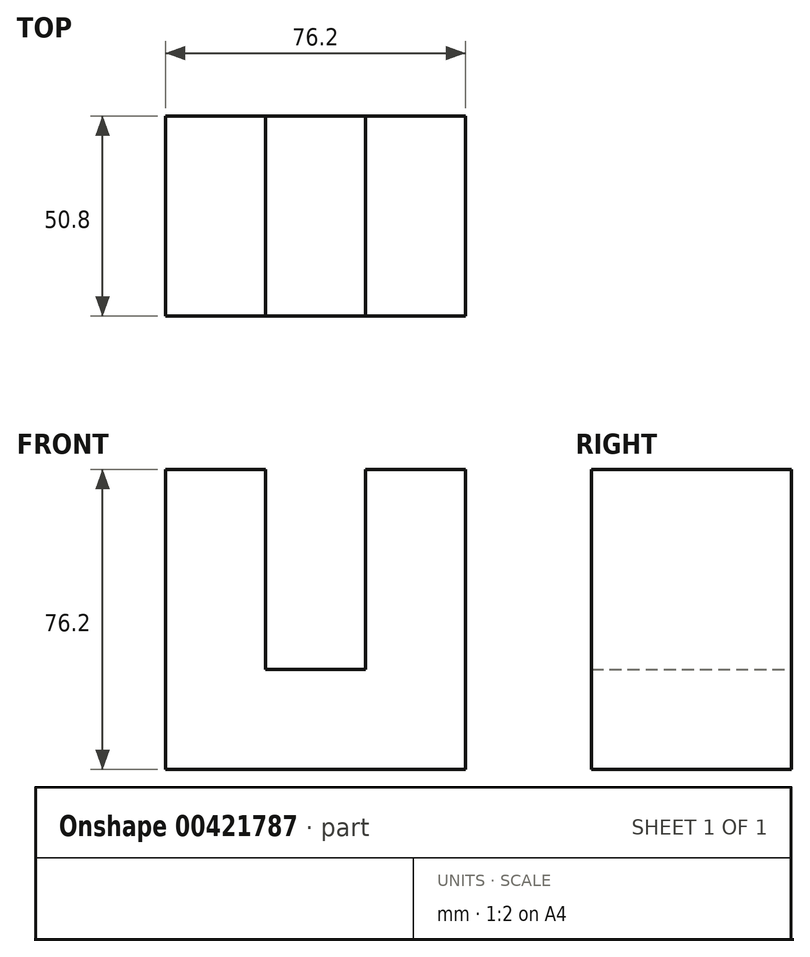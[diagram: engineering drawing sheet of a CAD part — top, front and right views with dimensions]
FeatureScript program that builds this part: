
annotation { "Feature Type Name" : "Feature", "Feature Type Description" : "" }
export const myFeature = defineFeature(function(context is Context, id is Id, definition is map)
    precondition{}
    {
        {
            var Q0;
            Q0=qCreatedBy(makeId("Front.planeOp"),FACE);
            var sketch = newSketch(context, id + "F0", { "sketchPlane" : qUnion([Q0])});
            skLineSegment(sketch, "E0", {"start": v(0, 0) * mm, "end": v(76.2, 0) * mm});
            skLineSegment(sketch, "E1", {"start": v(0, 0) * mm, "end": v(0, 76.2) * mm});
            skLineSegment(sketch, "E2", {"start": v(76.2, 0) * mm, "end": v(76.2, 76.2) * mm});
            skLineSegment(sketch, "E3", {"start": v(0, 76.2) * mm, "end": v(25.4, 76.2) * mm});
            skLineSegment(sketch, "E4", {"start": v(76.2, 76.2) * mm, "end": v(50.8, 76.2) * mm});
            skLineSegment(sketch, "E5", {"start": v(25.4, 76.2) * mm, "end": v(25.4, 25.4) * mm});
            skLineSegment(sketch, "E6", {"start": v(50.8, 76.2) * mm, "end": v(50.8, 25.4) * mm});
            skLineSegment(sketch, "E7", {"start": v(25.4, 25.4) * mm, "end": v(50.8, 25.4) * mm});
            skSolve(sketch);
        }
        {
            var Q0;
            Q0=makeQuery(id+"F0.imprint","IMPRINT",FACE,{"disambiguationData":[TD([[makeQuery(id+"F0.imprint","IMPRINT",EDGE,{"derivedFrom":sQuery(id+"F0.wireOp",EDGE,"E0")}),1.0]])]});
            extrude(context, id + "F1", {"entities" : qUnion([Q0]), "depth" : 50.8 * mm});
        }
    });
